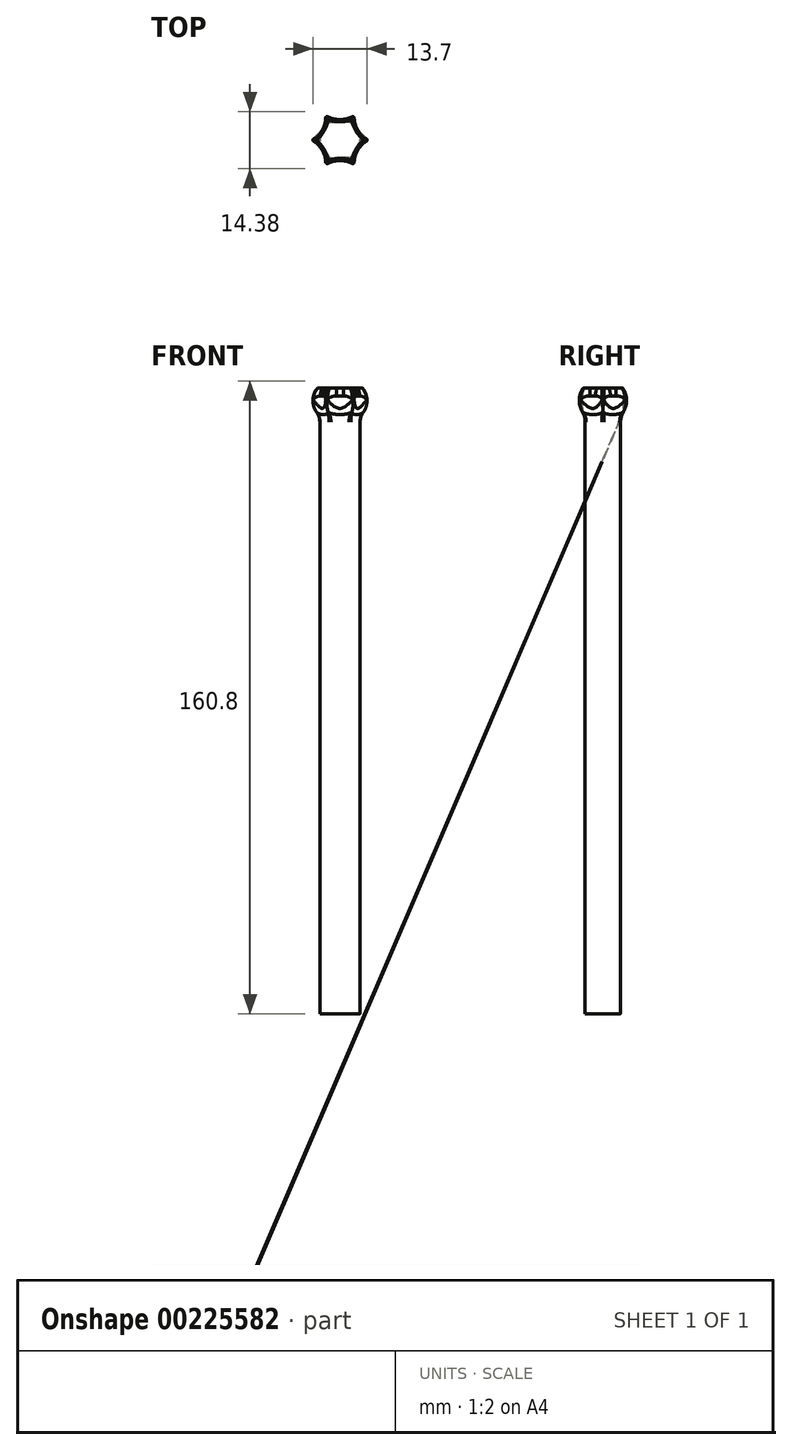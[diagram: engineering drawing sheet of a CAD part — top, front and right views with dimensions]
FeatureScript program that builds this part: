
annotation { "Feature Type Name" : "Feature", "Feature Type Description" : "" }
export const myFeature = defineFeature(function(context is Context, id is Id, definition is map)
    precondition{}
    {
        {
            var Q0;
            Q0=qCreatedBy(makeId("Top.planeOp"),FACE);
            var sketch = newSketch(context, id + "F0", { "sketchPlane" : qUnion([Q0])});
            skCircle(sketch, "E0.cCircle", {"center": v(0, 0) * mm, "radius": 6 * mm, "construction": true});
            skLineSegment(sketch, "E0.0", {"start": v(-3.46, 6) * mm, "end": v(3.46, 6) * mm});
            skLineSegment(sketch, "E0.1", {"start": v(3.46, 6) * mm, "end": v(6.93, 0) * mm});
            skLineSegment(sketch, "E0.2", {"start": v(6.93, 0) * mm, "end": v(3.46, -6) * mm});
            skLineSegment(sketch, "E0.3", {"start": v(3.46, -6) * mm, "end": v(-3.46, -6) * mm});
            skLineSegment(sketch, "E0.4", {"start": v(-3.46, -6) * mm, "end": v(-6.93, 0) * mm});
            skLineSegment(sketch, "E0.5", {"start": v(-6.93, 0) * mm, "end": v(-3.46, 6) * mm});
            skPoint(sketch, "E0.0.midPoint", {"position": v(0, 6) * mm});
            skSolve(sketch);
        }
        {
            var Q0;
            Q0=makeQuery(id+"F0.imprint","IMPRINT",FACE,{"disambiguationData":[TD([[makeQuery(id+"F0.imprint","IMPRINT",EDGE,{"derivedFrom":sQuery(id+"F0.wireOp",EDGE,"E0.0")}),-1.0]])]});
            extrude(context, id + "F1", {"entities" : qUnion([Q0]), "depth" : 20 * mm});
        }
        {
            var Q0;
            Q0=makeQuery(id+"F1.opExtrude","CAP_FACE",FACE,{"disambiguationData":[OSD([sQuery(id+"F0.wireOp",EDGE,"E0.0"),sQuery(id+"F0.wireOp",EDGE,"E0.1"),sQuery(id+"F0.wireOp",EDGE,"E0.2"),sQuery(id+"F0.wireOp",EDGE,"E0.3"),sQuery(id+"F0.wireOp",EDGE,"E0.4"),sQuery(id+"F0.wireOp",EDGE,"E0.5")])],"isStart":false});
            var sketch = newSketch(context, id + "F2", { "sketchPlane" : qUnion([Q0])});
            skCircle(sketch, "E1.cCircle", {"center": v(0, 0) * mm, "radius": 4.5 * mm, "construction": true});
            skLineSegment(sketch, "E1.0", {"start": v(-2.6, 4.5) * mm, "end": v(2.6, 4.5) * mm});
            skLineSegment(sketch, "E1.1", {"start": v(2.6, 4.5) * mm, "end": v(5.2, 0) * mm});
            skLineSegment(sketch, "E1.2", {"start": v(5.2, 0) * mm, "end": v(2.6, -4.5) * mm});
            skLineSegment(sketch, "E1.3", {"start": v(2.6, -4.5) * mm, "end": v(-2.6, -4.5) * mm});
            skLineSegment(sketch, "E1.4", {"start": v(-2.6, -4.5) * mm, "end": v(-5.2, 0) * mm});
            skLineSegment(sketch, "E1.5", {"start": v(-5.2, 0) * mm, "end": v(-2.6, 4.5) * mm});
            skPoint(sketch, "E1.0.midPoint", {"position": v(0, 4.5) * mm});
            skSolve(sketch);
        }
        {
            var Q0;
            Q0=makeQuery(id+"F2.imprint","IMPRINT",FACE,{"disambiguationData":[TD([[makeQuery(id+"F2.imprint","IMPRINT",EDGE,{"derivedFrom":sQuery(id+"F2.wireOp",EDGE,"E1.0")}),-1.0]])]});
            extrude(context, id + "F3", {"entities" : qUnion([Q0]), "operationType" : NewBodyOperationType.ADD, "depth" : 3 * mm});
        }
        {
            var Q0;
            Q0=makeQuery(id+"F3.opExtrude","CAP_FACE",FACE,{"disambiguationData":[OSD([sQuery(id+"F2.wireOp",EDGE,"E1.0"),sQuery(id+"F2.wireOp",EDGE,"E1.1"),sQuery(id+"F2.wireOp",EDGE,"E1.2"),sQuery(id+"F2.wireOp",EDGE,"E1.3"),sQuery(id+"F2.wireOp",EDGE,"E1.4"),sQuery(id+"F2.wireOp",EDGE,"E1.5")])],"isStart":false});
            var sketch = newSketch(context, id + "F4", { "sketchPlane" : qUnion([Q0])});
            skCircle(sketch, "E2.cCircle", {"center": v(0, 0) * mm, "radius": 6 * mm, "construction": true});
            skPoint(sketch, "E2.cCircle.perimeterSnap0", {"position": v(0, 4.5) * mm});
            skLineSegment(sketch, "E2.0", {"start": v(-3.46, 6) * mm, "end": v(3.46, 6) * mm});
            skLineSegment(sketch, "E2.1", {"start": v(3.46, 6) * mm, "end": v(6.93, 0) * mm});
            skLineSegment(sketch, "E2.2", {"start": v(6.93, 0) * mm, "end": v(3.46, -6) * mm});
            skLineSegment(sketch, "E2.3", {"start": v(3.46, -6) * mm, "end": v(-3.46, -6) * mm});
            skLineSegment(sketch, "E2.4", {"start": v(-3.46, -6) * mm, "end": v(-6.93, 0) * mm});
            skLineSegment(sketch, "E2.5", {"start": v(-6.93, 0) * mm, "end": v(-3.46, 6) * mm});
            skPoint(sketch, "E2.0.midPoint", {"position": v(0, 6) * mm});
            skPoint(sketch, "E2.0.midPoint.positionSnap0", {"position": v(0, 4.5) * mm});
            skSolve(sketch);
        }
        {
            var Q0;
            Q0=makeQuery(id+"F4.imprint","IMPRINT",FACE,{"disambiguationData":[TD([[makeQuery(id+"F4.imprint","IMPRINT",EDGE,{"derivedFrom":sQuery(id+"F4.wireOp",EDGE,"E2.0")}),-1.0]])]});
            var Q1;
            Q1=makeQuery(id+"F4.imprint","IMPRINT",FACE,{"disambiguationData":[TD([[makeQuery(id+"F4.imprint","IMPRINT",EDGE,{"derivedFrom":makeQuery(id+"F3.opExtrude","CAP_EDGE",EDGE,{"disambiguationData":[OSD([sQuery(id+"F2.wireOp",EDGE,"E1.0")])],"isStart":false})}),-1.0]])]});
            extrude(context, id + "F5", {"entities" : qUnion([Q0, Q1]), "operationType" : NewBodyOperationType.ADD, "depth" : 9 * mm});
        }
        {
            var Q0;
            Q0=makeQuery(id+"F5.opExtrude","CAP_EDGE",EDGE,{"disambiguationData":[OSD([sQuery(id+"F4.wireOp",EDGE,"E2.3")])],"isStart":true});
            var Q1;
            Q1=makeQuery(id+"F5.opExtrude","CAP_EDGE",EDGE,{"disambiguationData":[OSD([sQuery(id+"F4.wireOp",EDGE,"E2.2")])],"isStart":true});
            var Q2;
            Q2=makeQuery(id+"F5.opExtrude","CAP_EDGE",EDGE,{"disambiguationData":[OSD([sQuery(id+"F4.wireOp",EDGE,"E2.0")])],"isStart":true});
            var Q3;
            Q3=makeQuery(id+"F5.opExtrude","CAP_EDGE",EDGE,{"disambiguationData":[OSD([sQuery(id+"F4.wireOp",EDGE,"E2.5")])],"isStart":true});
            var Q4;
            Q4=makeQuery(id+"F5.opExtrude","CAP_EDGE",EDGE,{"disambiguationData":[OSD([sQuery(id+"F4.wireOp",EDGE,"E2.1")])],"isStart":true});
            var Q5;
            Q5=makeQuery(id+"F5.opExtrude","CAP_EDGE",EDGE,{"disambiguationData":[OSD([sQuery(id+"F4.wireOp",EDGE,"E2.4")])],"isStart":true});
            var Q6;
            Q6=makeQuery(id+"F5.opExtrude","CAP_EDGE",EDGE,{"disambiguationData":[OSD([sQuery(id+"F4.wireOp",EDGE,"E2.3")])],"isStart":false});
            var Q7;
            Q7=makeQuery(id+"F5.opExtrude","CAP_EDGE",EDGE,{"disambiguationData":[OSD([sQuery(id+"F4.wireOp",EDGE,"E2.4")])],"isStart":false});
            var Q8;
            Q8=makeQuery(id+"F5.opExtrude","CAP_EDGE",EDGE,{"disambiguationData":[OSD([sQuery(id+"F4.wireOp",EDGE,"E2.2")])],"isStart":false});
            var Q9;
            Q9=makeQuery(id+"F5.opExtrude","CAP_EDGE",EDGE,{"disambiguationData":[OSD([sQuery(id+"F4.wireOp",EDGE,"E2.1")])],"isStart":false});
            var Q10;
            Q10=makeQuery(id+"F5.opExtrude","CAP_EDGE",EDGE,{"disambiguationData":[OSD([sQuery(id+"F4.wireOp",EDGE,"E2.5")])],"isStart":false});
            var Q11;
            Q11=makeQuery(id+"F5.opExtrude","CAP_EDGE",EDGE,{"disambiguationData":[OSD([sQuery(id+"F4.wireOp",EDGE,"E2.0")])],"isStart":false});
            fillet(context, id + "F6", {"entities" : qUnion([Q0, Q1, Q2, Q3, Q4, Q5, Q6, Q7, Q8, Q9, Q10, Q11]), "radius" : 5 * mm, "allowEdgeOverflow" : false});
        }
        {
            var Q0;
            Q0=makeQuery(id+"F1.opExtrude","CAP_EDGE",EDGE,{"disambiguationData":[OSD([sQuery(id+"F0.wireOp",EDGE,"E0.1")])],"isStart":false});
            var Q1;
            Q1=makeQuery(id+"F1.opExtrude","CAP_EDGE",EDGE,{"disambiguationData":[OSD([sQuery(id+"F0.wireOp",EDGE,"E0.0")])],"isStart":false});
            var Q2;
            Q2=makeQuery(id+"F1.opExtrude","CAP_EDGE",EDGE,{"disambiguationData":[OSD([sQuery(id+"F0.wireOp",EDGE,"E0.5")])],"isStart":false});
            var Q3;
            Q3=makeQuery(id+"F1.opExtrude","CAP_EDGE",EDGE,{"disambiguationData":[OSD([sQuery(id+"F0.wireOp",EDGE,"E0.4")])],"isStart":false});
            var Q4;
            Q4=makeQuery(id+"F1.opExtrude","CAP_EDGE",EDGE,{"disambiguationData":[OSD([sQuery(id+"F0.wireOp",EDGE,"E0.3")])],"isStart":false});
            var Q5;
            Q5=makeQuery(id+"F1.opExtrude","CAP_EDGE",EDGE,{"disambiguationData":[OSD([sQuery(id+"F0.wireOp",EDGE,"E0.2")])],"isStart":false});
            chamfer(context, id + "F7", {"entities" : qUnion([Q0, Q1, Q2, Q3, Q4, Q5]), "chamferType" : ChamferType.TWO_OFFSETS, "width1" : 8 * mm, "oppositeDirection" : false, "width2" : 1.5 * mm, "tangentPropagation" : true});
        }
        {
            var Q0;
            {var subQ0=sQuery(id+"F0.wireOp",EDGE,"E0.3");Q0=makeQuery(id+"F7.opChamfer","BLEND_EDGE",EDGE,{"blendedFrom":[makeQuery(id+"F1.opExtrude","CAP_EDGE",EDGE,{"disambiguationData":[OSD([subQ0])],"isStart":false}),makeQuery(id+"F1.opExtrude","SWEPT_FACE",FACE,{"disambiguationData":[OSD([subQ0])]})],"blendedInto":[makeQuery(id+"F1.opExtrude","SWEPT_FACE",FACE,{"disambiguationData":[OSD([subQ0])]})]});}
            var Q1;
            {var subQ0=sQuery(id+"F0.wireOp",EDGE,"E0.2");Q1=makeQuery(id+"F7.opChamfer","BLEND_EDGE",EDGE,{"blendedFrom":[makeQuery(id+"F1.opExtrude","CAP_EDGE",EDGE,{"disambiguationData":[OSD([subQ0])],"isStart":false}),makeQuery(id+"F1.opExtrude","SWEPT_FACE",FACE,{"disambiguationData":[OSD([subQ0])]})],"blendedInto":[makeQuery(id+"F1.opExtrude","SWEPT_FACE",FACE,{"disambiguationData":[OSD([subQ0])]})]});}
            var Q2;
            {var subQ0=sQuery(id+"F0.wireOp",EDGE,"E0.1");Q2=makeQuery(id+"F7.opChamfer","BLEND_EDGE",EDGE,{"blendedFrom":[makeQuery(id+"F1.opExtrude","CAP_EDGE",EDGE,{"disambiguationData":[OSD([subQ0])],"isStart":false}),makeQuery(id+"F1.opExtrude","SWEPT_FACE",FACE,{"disambiguationData":[OSD([subQ0])]})],"blendedInto":[makeQuery(id+"F1.opExtrude","SWEPT_FACE",FACE,{"disambiguationData":[OSD([subQ0])]})]});}
            var Q3;
            {var subQ0=sQuery(id+"F0.wireOp",EDGE,"E0.0");Q3=makeQuery(id+"F7.opChamfer","BLEND_EDGE",EDGE,{"blendedFrom":[makeQuery(id+"F1.opExtrude","CAP_EDGE",EDGE,{"disambiguationData":[OSD([subQ0])],"isStart":false}),makeQuery(id+"F1.opExtrude","SWEPT_FACE",FACE,{"disambiguationData":[OSD([subQ0])]})],"blendedInto":[makeQuery(id+"F1.opExtrude","SWEPT_FACE",FACE,{"disambiguationData":[OSD([subQ0])]})]});}
            var Q4;
            {var subQ0=sQuery(id+"F0.wireOp",EDGE,"E0.5");Q4=makeQuery(id+"F7.opChamfer","BLEND_EDGE",EDGE,{"blendedFrom":[makeQuery(id+"F1.opExtrude","CAP_EDGE",EDGE,{"disambiguationData":[OSD([subQ0])],"isStart":false}),makeQuery(id+"F1.opExtrude","SWEPT_FACE",FACE,{"disambiguationData":[OSD([subQ0])]})],"blendedInto":[makeQuery(id+"F1.opExtrude","SWEPT_FACE",FACE,{"disambiguationData":[OSD([subQ0])]})]});}
            var Q5;
            {var subQ0=sQuery(id+"F0.wireOp",EDGE,"E0.4");Q5=makeQuery(id+"F7.opChamfer","BLEND_EDGE",EDGE,{"blendedFrom":[makeQuery(id+"F1.opExtrude","CAP_EDGE",EDGE,{"disambiguationData":[OSD([subQ0])],"isStart":false}),makeQuery(id+"F1.opExtrude","SWEPT_FACE",FACE,{"disambiguationData":[OSD([subQ0])]})],"blendedInto":[makeQuery(id+"F1.opExtrude","SWEPT_FACE",FACE,{"disambiguationData":[OSD([subQ0])]})]});}
            fillet(context, id + "F8", {"entities" : qUnion([Q0, Q1, Q2, Q3, Q4, Q5]), "radius" : 30 * mm, "tangentPropagation" : true, "allowEdgeOverflow" : false});
        }
        {
            var Q0;
            Q0=makeQuery(id+"F6.opFillet","BLEND_EDGE",EDGE,{"blendedFrom":[makeQuery(id+"F5.opExtrude","CAP_EDGE",EDGE,{"disambiguationData":[OSD([sQuery(id+"F4.wireOp",EDGE,"E2.4")])],"isStart":true}),makeQuery(id+"F3.opExtrude","SWEPT_FACE",FACE,{"disambiguationData":[OSD([sQuery(id+"F2.wireOp",EDGE,"E1.4")])]})],"blendedInto":[makeQuery(id+"F3.opExtrude","SWEPT_FACE",FACE,{"disambiguationData":[OSD([sQuery(id+"F2.wireOp",EDGE,"E1.4")])]})]});
            var Q1;
            Q1=makeQuery(id+"F6.opFillet","BLEND_EDGE",EDGE,{"blendedFrom":[makeQuery(id+"F5.opExtrude","CAP_EDGE",EDGE,{"disambiguationData":[OSD([sQuery(id+"F4.wireOp",EDGE,"E2.5")])],"isStart":true}),makeQuery(id+"F3.opExtrude","SWEPT_FACE",FACE,{"disambiguationData":[OSD([sQuery(id+"F2.wireOp",EDGE,"E1.5")])]})],"blendedInto":[makeQuery(id+"F3.opExtrude","SWEPT_FACE",FACE,{"disambiguationData":[OSD([sQuery(id+"F2.wireOp",EDGE,"E1.5")])]})]});
            var Q2;
            Q2=makeQuery(id+"F6.opFillet","BLEND_EDGE",EDGE,{"blendedFrom":[makeQuery(id+"F5.opExtrude","CAP_EDGE",EDGE,{"disambiguationData":[OSD([sQuery(id+"F4.wireOp",EDGE,"E2.0")])],"isStart":true}),makeQuery(id+"F3.opExtrude","SWEPT_FACE",FACE,{"disambiguationData":[OSD([sQuery(id+"F2.wireOp",EDGE,"E1.0")])]})],"blendedInto":[makeQuery(id+"F3.opExtrude","SWEPT_FACE",FACE,{"disambiguationData":[OSD([sQuery(id+"F2.wireOp",EDGE,"E1.0")])]})]});
            var Q3;
            Q3=makeQuery(id+"F6.opFillet","BLEND_EDGE",EDGE,{"blendedFrom":[makeQuery(id+"F5.opExtrude","CAP_EDGE",EDGE,{"disambiguationData":[OSD([sQuery(id+"F4.wireOp",EDGE,"E2.1")])],"isStart":true}),makeQuery(id+"F3.opExtrude","SWEPT_FACE",FACE,{"disambiguationData":[OSD([sQuery(id+"F2.wireOp",EDGE,"E1.1")])]})],"blendedInto":[makeQuery(id+"F3.opExtrude","SWEPT_FACE",FACE,{"disambiguationData":[OSD([sQuery(id+"F2.wireOp",EDGE,"E1.1")])]})]});
            var Q4;
            Q4=makeQuery(id+"F6.opFillet","BLEND_EDGE",EDGE,{"blendedFrom":[makeQuery(id+"F5.opExtrude","CAP_EDGE",EDGE,{"disambiguationData":[OSD([sQuery(id+"F4.wireOp",EDGE,"E2.2")])],"isStart":true}),makeQuery(id+"F3.opExtrude","SWEPT_FACE",FACE,{"disambiguationData":[OSD([sQuery(id+"F2.wireOp",EDGE,"E1.2")])]})],"blendedInto":[makeQuery(id+"F3.opExtrude","SWEPT_FACE",FACE,{"disambiguationData":[OSD([sQuery(id+"F2.wireOp",EDGE,"E1.2")])]})]});
            var Q5;
            Q5=makeQuery(id+"F6.opFillet","BLEND_EDGE",EDGE,{"blendedFrom":[makeQuery(id+"F5.opExtrude","CAP_EDGE",EDGE,{"disambiguationData":[OSD([sQuery(id+"F4.wireOp",EDGE,"E2.3")])],"isStart":true}),makeQuery(id+"F3.opExtrude","SWEPT_FACE",FACE,{"disambiguationData":[OSD([sQuery(id+"F2.wireOp",EDGE,"E1.3")])]})],"blendedInto":[makeQuery(id+"F3.opExtrude","SWEPT_FACE",FACE,{"disambiguationData":[OSD([sQuery(id+"F2.wireOp",EDGE,"E1.3")])]})]});
            fillet(context, id + "F9", {"entities" : qUnion([Q0, Q1, Q2, Q3, Q4, Q5]), "radius" : 5 * mm, "tangentPropagation" : true, "allowEdgeOverflow" : false});
        }
        {
            var Q0;
            Q0=makeQuery(id+"F6.opFillet","BLEND_EDGE",EDGE,{"blendedFrom":[makeQuery(id+"F5.opExtrude","CAP_EDGE",EDGE,{"disambiguationData":[OSD([sQuery(id+"F4.wireOp",EDGE,"E2.4")])],"isStart":false}),makeQuery(id+"F5.opExtrude","CAP_EDGE",EDGE,{"disambiguationData":[OSD([sQuery(id+"F4.wireOp",EDGE,"E2.5")])],"isStart":false})],"blendedInto":[]});
            var Q1;
            Q1=makeQuery(id+"F7.opChamfer","BLEND_EDGE",EDGE,{"blendedFrom":[makeQuery(id+"F1.opExtrude","CAP_EDGE",EDGE,{"disambiguationData":[OSD([sQuery(id+"F0.wireOp",EDGE,"E0.4")])],"isStart":false}),makeQuery(id+"F1.opExtrude","CAP_EDGE",EDGE,{"disambiguationData":[OSD([sQuery(id+"F0.wireOp",EDGE,"E0.5")])],"isStart":false})],"blendedInto":[]});
            var Q2;
            Q2=makeQuery(id+"F7.opChamfer","BLEND_EDGE",EDGE,{"blendedFrom":[makeQuery(id+"F1.opExtrude","CAP_EDGE",EDGE,{"disambiguationData":[OSD([sQuery(id+"F0.wireOp",EDGE,"E0.3")])],"isStart":false}),makeQuery(id+"F1.opExtrude","CAP_EDGE",EDGE,{"disambiguationData":[OSD([sQuery(id+"F0.wireOp",EDGE,"E0.4")])],"isStart":false})],"blendedInto":[]});
            var Q3;
            Q3=makeQuery(id+"F6.opFillet","BLEND_EDGE",EDGE,{"blendedFrom":[makeQuery(id+"F5.opExtrude","CAP_EDGE",EDGE,{"disambiguationData":[OSD([sQuery(id+"F4.wireOp",EDGE,"E2.3")])],"isStart":false}),makeQuery(id+"F5.opExtrude","CAP_EDGE",EDGE,{"disambiguationData":[OSD([sQuery(id+"F4.wireOp",EDGE,"E2.4")])],"isStart":false})],"blendedInto":[]});
            var Q4;
            Q4=makeQuery(id+"F6.opFillet","BLEND_EDGE",EDGE,{"blendedFrom":[makeQuery(id+"F5.opExtrude","CAP_EDGE",EDGE,{"disambiguationData":[OSD([sQuery(id+"F4.wireOp",EDGE,"E2.2")])],"isStart":false}),makeQuery(id+"F5.opExtrude","CAP_EDGE",EDGE,{"disambiguationData":[OSD([sQuery(id+"F4.wireOp",EDGE,"E2.3")])],"isStart":false})],"blendedInto":[]});
            var Q5;
            Q5=makeQuery(id+"F7.opChamfer","BLEND_EDGE",EDGE,{"blendedFrom":[makeQuery(id+"F1.opExtrude","CAP_EDGE",EDGE,{"disambiguationData":[OSD([sQuery(id+"F0.wireOp",EDGE,"E0.2")])],"isStart":false}),makeQuery(id+"F1.opExtrude","CAP_EDGE",EDGE,{"disambiguationData":[OSD([sQuery(id+"F0.wireOp",EDGE,"E0.3")])],"isStart":false})],"blendedInto":[]});
            var Q6;
            Q6=makeQuery(id+"F7.opChamfer","BLEND_EDGE",EDGE,{"blendedFrom":[makeQuery(id+"F1.opExtrude","CAP_EDGE",EDGE,{"disambiguationData":[OSD([sQuery(id+"F0.wireOp",EDGE,"E0.1")])],"isStart":false}),makeQuery(id+"F1.opExtrude","CAP_EDGE",EDGE,{"disambiguationData":[OSD([sQuery(id+"F0.wireOp",EDGE,"E0.2")])],"isStart":false})],"blendedInto":[]});
            var Q7;
            Q7=makeQuery(id+"F6.opFillet","BLEND_EDGE",EDGE,{"blendedFrom":[makeQuery(id+"F5.opExtrude","CAP_EDGE",EDGE,{"disambiguationData":[OSD([sQuery(id+"F4.wireOp",EDGE,"E2.1")])],"isStart":false}),makeQuery(id+"F5.opExtrude","CAP_EDGE",EDGE,{"disambiguationData":[OSD([sQuery(id+"F4.wireOp",EDGE,"E2.2")])],"isStart":false})],"blendedInto":[]});
            var Q8;
            Q8=makeQuery(id+"F7.opChamfer","BLEND_EDGE",EDGE,{"blendedFrom":[makeQuery(id+"F1.opExtrude","CAP_EDGE",EDGE,{"disambiguationData":[OSD([sQuery(id+"F0.wireOp",EDGE,"E0.0")])],"isStart":false}),makeQuery(id+"F1.opExtrude","CAP_EDGE",EDGE,{"disambiguationData":[OSD([sQuery(id+"F0.wireOp",EDGE,"E0.1")])],"isStart":false})],"blendedInto":[]});
            var Q9;
            Q9=makeQuery(id+"F6.opFillet","BLEND_EDGE",EDGE,{"blendedFrom":[makeQuery(id+"F5.opExtrude","CAP_EDGE",EDGE,{"disambiguationData":[OSD([sQuery(id+"F4.wireOp",EDGE,"E2.0")])],"isStart":false}),makeQuery(id+"F5.opExtrude","CAP_EDGE",EDGE,{"disambiguationData":[OSD([sQuery(id+"F4.wireOp",EDGE,"E2.1")])],"isStart":false})],"blendedInto":[]});
            var Q10;
            Q10=makeQuery(id+"F6.opFillet","BLEND_EDGE",EDGE,{"blendedFrom":[makeQuery(id+"F5.opExtrude","CAP_EDGE",EDGE,{"disambiguationData":[OSD([sQuery(id+"F4.wireOp",EDGE,"E2.0")])],"isStart":false}),makeQuery(id+"F5.opExtrude","CAP_EDGE",EDGE,{"disambiguationData":[OSD([sQuery(id+"F4.wireOp",EDGE,"E2.5")])],"isStart":false})],"blendedInto":[]});
            var Q11;
            Q11=makeQuery(id+"F7.opChamfer","BLEND_EDGE",EDGE,{"blendedFrom":[makeQuery(id+"F1.opExtrude","CAP_EDGE",EDGE,{"disambiguationData":[OSD([sQuery(id+"F0.wireOp",EDGE,"E0.0")])],"isStart":false}),makeQuery(id+"F1.opExtrude","CAP_EDGE",EDGE,{"disambiguationData":[OSD([sQuery(id+"F0.wireOp",EDGE,"E0.5")])],"isStart":false})],"blendedInto":[]});
            fillet(context, id + "F10", {"entities" : qUnion([Q0, Q1, Q2, Q3, Q4, Q5, Q6, Q7, Q8, Q9, Q10, Q11]), "radius" : 0.5 * mm, "tangentPropagation" : true, "allowEdgeOverflow" : false});
        }
        {
            var Q0;
            Q0=makeQuery(id+"F7.opChamfer","BLEND_EDGE",EDGE,{"blendedFrom":[makeQuery(id+"F1.opExtrude","CAP_EDGE",EDGE,{"disambiguationData":[OSD([sQuery(id+"F0.wireOp",EDGE,"E0.2")])],"isStart":false}),makeQuery(id+"F3.opExtrude","SWEPT_FACE",FACE,{"disambiguationData":[OSD([sQuery(id+"F2.wireOp",EDGE,"E1.2")])]})],"blendedInto":[makeQuery(id+"F3.opExtrude","SWEPT_FACE",FACE,{"disambiguationData":[OSD([sQuery(id+"F2.wireOp",EDGE,"E1.2")])]})]});
            fillet(context, id + "F11", {"entities" : qUnion([Q0]), "radius" : 5 * mm, "tangentPropagation" : true, "allowEdgeOverflow" : false});
        }
        {
            var Q0;
            Q0=makeQuery(id+"F5.opExtrude","CAP_FACE",FACE,{"disambiguationData":[OSD([sQuery(id+"F4.wireOp",EDGE,"E2.0"),sQuery(id+"F4.wireOp",EDGE,"E2.1"),sQuery(id+"F4.wireOp",EDGE,"E2.2"),sQuery(id+"F4.wireOp",EDGE,"E2.3"),sQuery(id+"F4.wireOp",EDGE,"E2.4"),sQuery(id+"F4.wireOp",EDGE,"E2.5")])],"isStart":false});
            var sketch = newSketch(context, id + "F12", { "sketchPlane" : qUnion([Q0])});
            skArc(sketch, "E3", {"start": v(-6.78, 0.25) * mm, "mid": v(-4.5, 2.6) * mm, "end": v(-3.6, 5.75) * mm});
            skArc(sketch, "E4", {"start": v(-3.18, 6) * mm, "mid": v(0, 5.2) * mm, "end": v(3.18, 6) * mm});
            skArc(sketch, "E5", {"start": v(3.6, 5.75) * mm, "mid": v(4.5, 2.6) * mm, "end": v(6.78, 0.25) * mm});
            skArc(sketch, "E6", {"start": v(6.78, -0.25) * mm, "mid": v(4.5, -2.6) * mm, "end": v(3.6, -5.75) * mm});
            skArc(sketch, "E7", {"start": v(3.18, -6) * mm, "mid": v(0, -5.2) * mm, "end": v(-3.18, -6) * mm});
            skArc(sketch, "E8", {"start": v(-3.6, -5.75) * mm, "mid": v(-4.5, -2.6) * mm, "end": v(-6.78, -0.25) * mm});
            skLineSegment(sketch, "E9", {"start": v(-6.78, 0.25) * mm, "end": v(-3.6, 5.75) * mm});
            skLineSegment(sketch, "E10", {"start": v(-3.18, 6) * mm, "end": v(3.18, 6) * mm});
            skLineSegment(sketch, "E11", {"start": v(3.6, 5.75) * mm, "end": v(6.78, 0.25) * mm});
            skLineSegment(sketch, "E12", {"start": v(6.78, -0.25) * mm, "end": v(3.6, -5.75) * mm});
            skLineSegment(sketch, "E13", {"start": v(3.18, -6) * mm, "end": v(-3.18, -6) * mm});
            skLineSegment(sketch, "E14", {"start": v(-3.6, -5.75) * mm, "end": v(-6.78, -0.25) * mm});
            skSolve(sketch);
        }
        {
            var Q0;
            Q0=makeQuery(id+"F12.imprint","IMPRINT",FACE,{"disambiguationData":[TD([[makeQuery(id+"F12.imprint","IMPRINT",EDGE,{"derivedFrom":sQuery(id+"F12.wireOp",EDGE,"E3")}),1.0]])]});
            var Q1;
            Q1=makeQuery(id+"F12.imprint","IMPRINT",FACE,{"disambiguationData":[TD([[makeQuery(id+"F12.imprint","IMPRINT",EDGE,{"derivedFrom":sQuery(id+"F12.wireOp",EDGE,"E4")}),1.0]])]});
            var Q2;
            Q2=makeQuery(id+"F12.imprint","IMPRINT",FACE,{"disambiguationData":[TD([[makeQuery(id+"F12.imprint","IMPRINT",EDGE,{"derivedFrom":sQuery(id+"F12.wireOp",EDGE,"E5")}),1.0]])]});
            var Q3;
            Q3=makeQuery(id+"F12.imprint","IMPRINT",FACE,{"disambiguationData":[TD([[makeQuery(id+"F12.imprint","IMPRINT",EDGE,{"derivedFrom":sQuery(id+"F12.wireOp",EDGE,"E6")}),1.0]])]});
            var Q4;
            Q4=makeQuery(id+"F12.imprint","IMPRINT",FACE,{"disambiguationData":[TD([[makeQuery(id+"F12.imprint","IMPRINT",EDGE,{"derivedFrom":sQuery(id+"F12.wireOp",EDGE,"E7")}),1.0]])]});
            var Q5;
            Q5=makeQuery(id+"F12.imprint","IMPRINT",FACE,{"disambiguationData":[TD([[makeQuery(id+"F12.imprint","IMPRINT",EDGE,{"derivedFrom":sQuery(id+"F12.wireOp",EDGE,"E8")}),1.0]])]});
            extrude(context, id + "F13", {"entities" : qUnion([Q0, Q1, Q2, Q3, Q4, Q5]), "operationType" : NewBodyOperationType.REMOVE, "oppositeDirection" : true, "depth" : 10 * mm});
        }
        {
            var Q0;
            {var subQ0=sQuery(id+"F4.wireOp",EDGE,"E2.1");Q0=makeQuery(id+"F13.boolean.opBoolean","INTERSECT",EDGE,{"derivedFrom":[makeQuery(id+"F6.opFillet","BLEND_FACE",FACE,{"disambiguationData":[OSD([subQ0]),TDD([makeQuery(id+"F5.opExtrude","CAP_EDGE",EDGE,{"disambiguationData":[OSD([subQ0])],"isStart":false})])]}),makeQuery(id+"F13.opExtrude","SWEPT_FACE",FACE,{"disambiguationData":[OSD([sQuery(id+"F12.wireOp",EDGE,"E5")])]})]});}
            var Q1;
            {var subQ0=sQuery(id+"F4.wireOp",EDGE,"E2.0");Q1=makeQuery(id+"F13.boolean.opBoolean","INTERSECT",EDGE,{"derivedFrom":[makeQuery(id+"F6.opFillet","BLEND_FACE",FACE,{"disambiguationData":[OSD([subQ0]),TDD([makeQuery(id+"F5.opExtrude","CAP_EDGE",EDGE,{"disambiguationData":[OSD([subQ0])],"isStart":false})])]}),makeQuery(id+"F13.opExtrude","SWEPT_FACE",FACE,{"disambiguationData":[OSD([sQuery(id+"F12.wireOp",EDGE,"E4")])]})]});}
            var Q2;
            {var subQ0=sQuery(id+"F4.wireOp",EDGE,"E2.5");Q2=makeQuery(id+"F13.boolean.opBoolean","INTERSECT",EDGE,{"derivedFrom":[makeQuery(id+"F6.opFillet","BLEND_FACE",FACE,{"disambiguationData":[OSD([subQ0]),TDD([makeQuery(id+"F5.opExtrude","CAP_EDGE",EDGE,{"disambiguationData":[OSD([subQ0])],"isStart":false})])]}),makeQuery(id+"F13.opExtrude","SWEPT_FACE",FACE,{"disambiguationData":[OSD([sQuery(id+"F12.wireOp",EDGE,"E3")])]})]});}
            var Q3;
            {var subQ0=sQuery(id+"F4.wireOp",EDGE,"E2.4");Q3=makeQuery(id+"F13.boolean.opBoolean","INTERSECT",EDGE,{"derivedFrom":[makeQuery(id+"F6.opFillet","BLEND_FACE",FACE,{"disambiguationData":[OSD([subQ0]),TDD([makeQuery(id+"F5.opExtrude","CAP_EDGE",EDGE,{"disambiguationData":[OSD([subQ0])],"isStart":false})])]}),makeQuery(id+"F13.opExtrude","SWEPT_FACE",FACE,{"disambiguationData":[OSD([sQuery(id+"F12.wireOp",EDGE,"E8")])]})]});}
            var Q4;
            {var subQ0=sQuery(id+"F4.wireOp",EDGE,"E2.3");Q4=makeQuery(id+"F13.boolean.opBoolean","INTERSECT",EDGE,{"derivedFrom":[makeQuery(id+"F6.opFillet","BLEND_FACE",FACE,{"disambiguationData":[OSD([subQ0]),TDD([makeQuery(id+"F5.opExtrude","CAP_EDGE",EDGE,{"disambiguationData":[OSD([subQ0])],"isStart":false})])]}),makeQuery(id+"F13.opExtrude","SWEPT_FACE",FACE,{"disambiguationData":[OSD([sQuery(id+"F12.wireOp",EDGE,"E7")])]})]});}
            var Q5;
            {var subQ0=sQuery(id+"F4.wireOp",EDGE,"E2.2");Q5=makeQuery(id+"F13.boolean.opBoolean","INTERSECT",EDGE,{"derivedFrom":[makeQuery(id+"F6.opFillet","BLEND_FACE",FACE,{"disambiguationData":[OSD([subQ0]),TDD([makeQuery(id+"F5.opExtrude","CAP_EDGE",EDGE,{"disambiguationData":[OSD([subQ0])],"isStart":false})])]}),makeQuery(id+"F13.opExtrude","SWEPT_FACE",FACE,{"disambiguationData":[OSD([sQuery(id+"F12.wireOp",EDGE,"E6")])]})]});}
            var Q6;
            Q6=makeQuery(id+"F13.boolean.opBoolean","INTERSECT",EDGE,{"derivedFrom":[makeQuery(id+"F9.opFillet","BLEND_FACE",FACE,{"disambiguationData":[OSD([sQuery(id+"F2.wireOp",EDGE,"E1.2"),sQuery(id+"F4.wireOp",EDGE,"E2.2")])]}),makeQuery(id+"F13.opExtrude","SWEPT_FACE",FACE,{"disambiguationData":[OSD([sQuery(id+"F12.wireOp",EDGE,"E6")])]})]});
            var Q7;
            Q7=makeQuery(id+"F13.boolean.opBoolean","INTERSECT",EDGE,{"derivedFrom":[makeQuery(id+"F9.opFillet","BLEND_FACE",FACE,{"disambiguationData":[OSD([sQuery(id+"F2.wireOp",EDGE,"E1.3"),sQuery(id+"F4.wireOp",EDGE,"E2.3")])]}),makeQuery(id+"F13.opExtrude","SWEPT_FACE",FACE,{"disambiguationData":[OSD([sQuery(id+"F12.wireOp",EDGE,"E7")])]})]});
            var Q8;
            Q8=makeQuery(id+"F13.boolean.opBoolean","INTERSECT",EDGE,{"derivedFrom":[makeQuery(id+"F9.opFillet","BLEND_FACE",FACE,{"disambiguationData":[OSD([sQuery(id+"F2.wireOp",EDGE,"E1.4"),sQuery(id+"F4.wireOp",EDGE,"E2.4")])]}),makeQuery(id+"F13.opExtrude","SWEPT_FACE",FACE,{"disambiguationData":[OSD([sQuery(id+"F12.wireOp",EDGE,"E8")])]})]});
            var Q9;
            Q9=makeQuery(id+"F13.boolean.opBoolean","INTERSECT",EDGE,{"derivedFrom":[makeQuery(id+"F9.opFillet","BLEND_FACE",FACE,{"disambiguationData":[OSD([sQuery(id+"F2.wireOp",EDGE,"E1.5"),sQuery(id+"F4.wireOp",EDGE,"E2.5")])]}),makeQuery(id+"F13.opExtrude","SWEPT_FACE",FACE,{"disambiguationData":[OSD([sQuery(id+"F12.wireOp",EDGE,"E3")])]})]});
            var Q10;
            Q10=makeQuery(id+"F13.boolean.opBoolean","INTERSECT",EDGE,{"derivedFrom":[makeQuery(id+"F9.opFillet","BLEND_FACE",FACE,{"disambiguationData":[OSD([sQuery(id+"F2.wireOp",EDGE,"E1.0"),sQuery(id+"F4.wireOp",EDGE,"E2.0")])]}),makeQuery(id+"F13.opExtrude","SWEPT_FACE",FACE,{"disambiguationData":[OSD([sQuery(id+"F12.wireOp",EDGE,"E4")])]})]});
            var Q11;
            Q11=makeQuery(id+"F13.boolean.opBoolean","INTERSECT",EDGE,{"derivedFrom":[makeQuery(id+"F9.opFillet","BLEND_FACE",FACE,{"disambiguationData":[OSD([sQuery(id+"F2.wireOp",EDGE,"E1.1"),sQuery(id+"F4.wireOp",EDGE,"E2.1")])]}),makeQuery(id+"F13.opExtrude","SWEPT_FACE",FACE,{"disambiguationData":[OSD([sQuery(id+"F12.wireOp",EDGE,"E5")])]})]});
            fillet(context, id + "F14", {"entities" : qUnion([Q0, Q1, Q2, Q3, Q4, Q5, Q6, Q7, Q8, Q9, Q10, Q11]), "radius" : 4 * mm, "allowEdgeOverflow" : false});
        }
        {
            var Q0;
            Q0=makeQuery(id+"F5.opExtrude","CAP_FACE",FACE,{"disambiguationData":[OSD([sQuery(id+"F4.wireOp",EDGE,"E2.0"),sQuery(id+"F4.wireOp",EDGE,"E2.1"),sQuery(id+"F4.wireOp",EDGE,"E2.2"),sQuery(id+"F4.wireOp",EDGE,"E2.3"),sQuery(id+"F4.wireOp",EDGE,"E2.4"),sQuery(id+"F4.wireOp",EDGE,"E2.5")])],"isStart":false});
            var sketch = newSketch(context, id + "F15", { "sketchPlane" : qUnion([Q0])});
            skCircle(sketch, "E15", {"center": v(0, 0) * mm, "radius": 8 * mm});
            skSolve(sketch);
        }
        {
            var Q0;
            Q0=makeQuery(id+"F15.imprint","IMPRINT",FACE,{"disambiguationData":[TD([[makeQuery(id+"F15.imprint","IMPRINT",EDGE,{"derivedFrom":sQuery(id+"F15.wireOp",EDGE,"E15")}),1.0]])]});
            var Q1;
            {var subQ0=sQuery(id+"F4.wireOp",EDGE,"E2.5");var subQ1=sQuery(id+"F4.wireOp",EDGE,"E2.4");var subQ2=sQuery(id+"F4.wireOp",EDGE,"E2.3");var subQ3=sQuery(id+"F4.wireOp",EDGE,"E2.2");var subQ4=sQuery(id+"F4.wireOp",EDGE,"E2.1");var subQ5=sQuery(id+"F4.wireOp",EDGE,"E2.0");var subQ6=makeQuery(id+"F5.opExtrude","CAP_FACE",FACE,{"disambiguationData":[OSD([subQ5,subQ4,subQ3,subQ2,subQ1,subQ0])],"isStart":false});Q1=makeQuery(id+"F15.imprint","IMPRINT",FACE,{"disambiguationData":[TD([[makeQuery(id+"F15.imprint","IMPRINT",EDGE,{"derivedFrom":makeQuery(id+"F6.opFillet","BLEND_EDGE",EDGE,{"blendedFrom":[makeQuery(id+"F5.opExtrude","CAP_EDGE",EDGE,{"disambiguationData":[OSD([subQ5])],"isStart":false}),subQ6],"blendedInto":[subQ6]})}),1.0]])]});}
            extrude(context, id + "F16", {"entities" : qUnion([Q0, Q1]), "operationType" : NewBodyOperationType.REMOVE, "oppositeDirection" : true, "depth" : 2 * mm});
        }
        {
            var Q0;
            Q0=makeQuery(id+"F1.opExtrude","CAP_FACE",FACE,{"disambiguationData":[OSD([sQuery(id+"F0.wireOp",EDGE,"E0.0"),sQuery(id+"F0.wireOp",EDGE,"E0.1"),sQuery(id+"F0.wireOp",EDGE,"E0.2"),sQuery(id+"F0.wireOp",EDGE,"E0.3"),sQuery(id+"F0.wireOp",EDGE,"E0.4"),sQuery(id+"F0.wireOp",EDGE,"E0.5")])],"isStart":true});
            extrude(context, id + "F17", {"entities" : qUnion([Q0]), "operationType" : NewBodyOperationType.REMOVE, "oppositeDirection" : true, "depth" : 21 * mm});
        }
        {
            var Q0;
            Q0=makeQuery(id+"F17.boolean.opBoolean","COPY",FACE,{"derivedFrom":makeQuery(id+"F17.opExtrude","CAP_FACE",FACE,{"disambiguationData":[OSD([sQuery(id+"F0.wireOp",EDGE,"E0.0"),sQuery(id+"F0.wireOp",EDGE,"E0.1"),sQuery(id+"F0.wireOp",EDGE,"E0.2"),sQuery(id+"F0.wireOp",EDGE,"E0.3"),sQuery(id+"F0.wireOp",EDGE,"E0.4"),sQuery(id+"F0.wireOp",EDGE,"E0.5")])],"isStart":false})});
            extrude(context, id + "F18", {"entities" : qUnion([Q0]), "operationType" : NewBodyOperationType.ADD, "depth" : 150 * mm});
        }
    });
